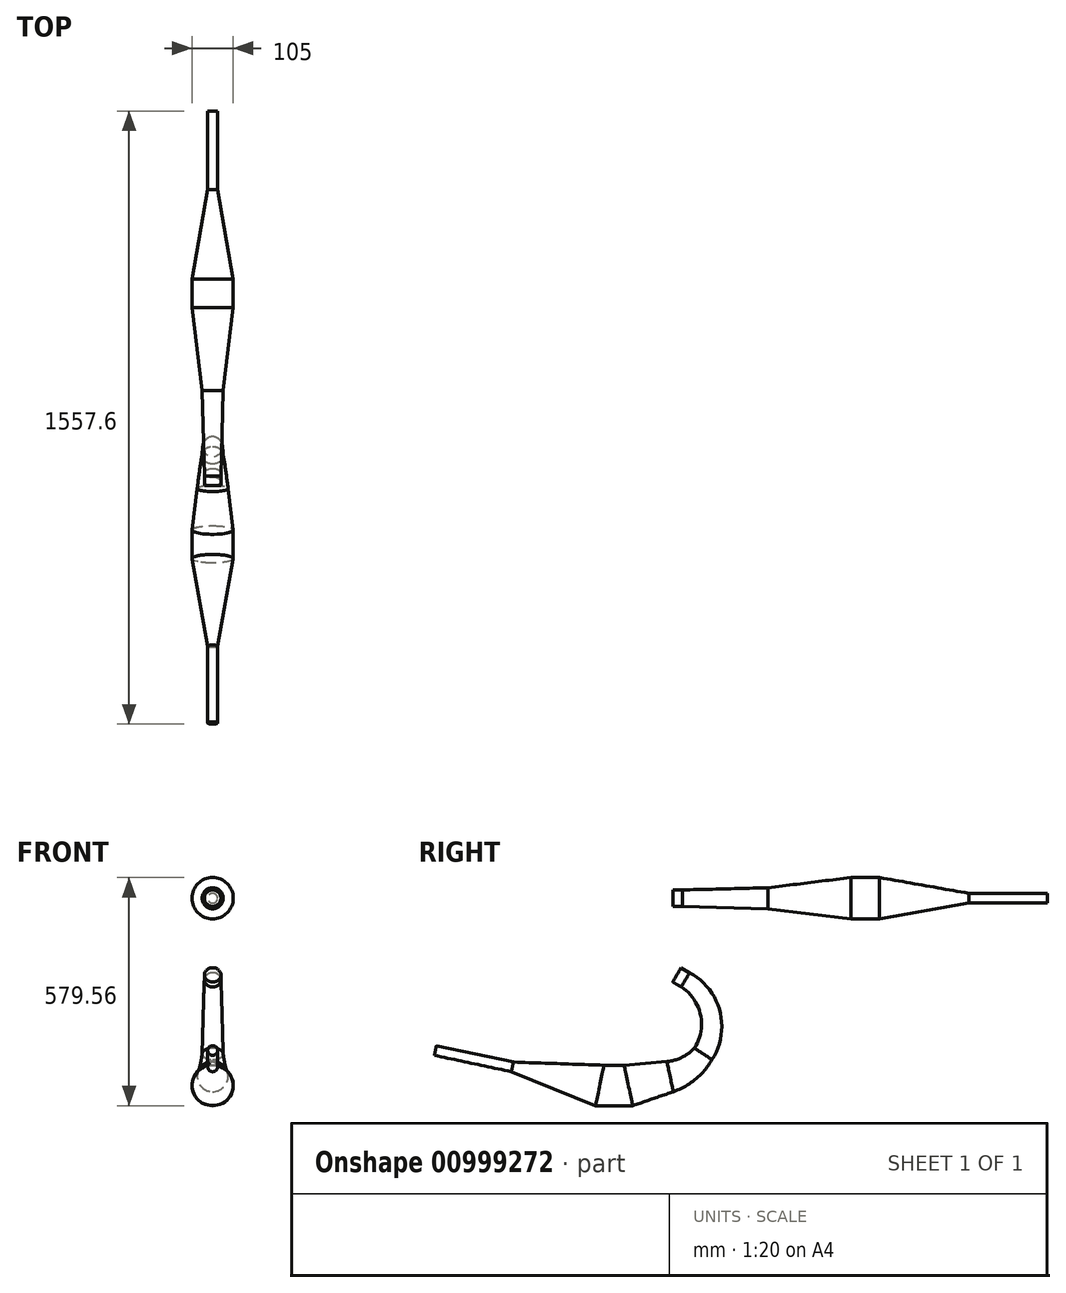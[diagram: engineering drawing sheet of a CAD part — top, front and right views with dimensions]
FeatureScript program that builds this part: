
annotation { "Feature Type Name" : "Feature", "Feature Type Description" : "" }
export const myFeature = defineFeature(function(context is Context, id is Id, definition is map)
    precondition{}
    {
        {
            var Q0;
            Q0=qCreatedBy(makeId("Right.planeOp"),FACE);
            var sketch = newSketch(context, id + "F0", { "sketchPlane" : qUnion([Q0])});
            skLineSegment(sketch, "E0", {"start": v(21.65, -12.5) * mm, "end": v(42.65, 23.87) * mm});
            skLineSegment(sketch, "E1", {"start": v(0, 191.98) * mm, "end": v(0, 233.98) * mm});
            skLineSegment(sketch, "E2", {"start": v(0, 212.98) * mm, "end": v(242, 212.98) * mm});
            skLineSegment(sketch, "E3", {"start": v(0, 212.98) * mm, "end": v(-65, 212.98) * mm});
            skLineSegment(sketch, "E4", {"start": v(242, 239.66) * mm, "end": v(242, 186.3) * mm});
            skLineSegment(sketch, "E5", {"start": v(25, 233.98) * mm, "end": v(242, 239.66) * mm});
            skLineSegment(sketch, "E6", {"start": v(25, 191.98) * mm, "end": v(242, 186.3) * mm});
            skLineSegment(sketch, "E7", {"start": v(-51.1, 50.44) * mm, "end": v(-51.1, 27.44) * mm});
            skLineSegment(sketch, "E8", {"start": v(-51.1, 38.94) * mm, "end": v(10.5, 18.19) * mm});
            skLineSegment(sketch, "E9", {"start": v(242, 212.98) * mm, "end": v(344.06, 212.98) * mm});
            skLineSegment(sketch, "E10", {"start": v(242, 239.66) * mm, "end": v(344.06, 252.2) * mm});
            skLineSegment(sketch, "E11", {"start": v(242, 186.3) * mm, "end": v(344.06, 173.76) * mm});
            skLineSegment(sketch, "E12", {"start": v(344.06, 252.2) * mm, "end": v(344.06, 173.76) * mm});
            skLineSegment(sketch, "E13", {"start": v(344.06, 212.98) * mm, "end": v(452.27, 212.98) * mm});
            skLineSegment(sketch, "E14", {"start": v(452.27, 160.48) * mm, "end": v(452.27, 265.48) * mm});
            skLineSegment(sketch, "E15", {"start": v(344.06, 252.2) * mm, "end": v(452.27, 265.48) * mm});
            skLineSegment(sketch, "E16", {"start": v(344.06, 173.76) * mm, "end": v(452.27, 160.48) * mm});
            skLineSegment(sketch, "E17", {"start": v(452.27, 212.98) * mm, "end": v(674, 212.98) * mm});
            skLineSegment(sketch, "E18", {"start": v(674, 212.98) * mm, "end": v(751.98, 212.98) * mm});
            skLineSegment(sketch, "E19", {"start": v(751.98, 200.48) * mm, "end": v(751.98, 225.48) * mm});
            skLineSegment(sketch, "E20", {"start": v(525.13, 265.48) * mm, "end": v(822.87, 212.98) * mm, "construction": true});
            skLineSegment(sketch, "E21", {"start": v(822.87, 212.98) * mm, "end": v(525.13, 160.48) * mm, "construction": true});
            skLineSegment(sketch, "E22", {"start": v(452.27, 265.48) * mm, "end": v(525.13, 265.48) * mm});
            skLineSegment(sketch, "E23", {"start": v(452.27, 160.48) * mm, "end": v(525.13, 160.48) * mm});
            skLineSegment(sketch, "E24", {"start": v(674, 186.73) * mm, "end": v(674, 239.23) * mm});
            skLineSegment(sketch, "E25", {"start": v(525.13, 265.48) * mm, "end": v(525.13, 160.48) * mm});
            skLineSegment(sketch, "E26", {"start": v(751.98, 225.48) * mm, "end": v(951.98, 225.48) * mm});
            skLineSegment(sketch, "E27", {"start": v(751.98, 200.48) * mm, "end": v(951.98, 200.48) * mm});
            skLineSegment(sketch, "E28", {"start": v(951.98, 200.48) * mm, "end": v(951.98, 225.48) * mm});
            skLineSegment(sketch, "E29", {"start": v(525.13, 265.48) * mm, "end": v(751.98, 225.48) * mm});
            skLineSegment(sketch, "E30", {"start": v(525.13, 160.48) * mm, "end": v(751.98, 200.48) * mm});
            skLineSegment(sketch, "E31", {"start": v(21.65, -12.5) * mm, "end": v(21.65, -190.3) * mm, "construction": true});
            skArc(sketch, "E32", {"start": v(32.15, 5.69) * mm, "mid": v(97.18, -130.66) * mm, "end": v(-6.8, -240.23) * mm, "construction": true});
            skLineSegment(sketch, "E33", {"start": v(-34.52, -109.8) * mm, "end": v(77.31, -182.43) * mm, "construction": true});
            skLineSegment(sketch, "E34", {"start": v(99.7, -196.96) * mm, "end": v(54.93, -167.9) * mm});
            skArc(sketch, "E35", {"start": v(99.7, -196.96) * mm, "mid": v(119.73, -74) * mm, "end": v(42.65, 23.87) * mm});
            skArc(sketch, "E36", {"start": v(54.93, -167.9) * mm, "mid": v(70.55, -83.29) * mm, "end": v(21.65, -12.5) * mm});
            skLineSegment(sketch, "E37", {"start": v(-6.8, -240.23) * mm, "end": v(-112.64, -262.73) * mm, "construction": true});
            skLineSegment(sketch, "E38", {"start": v(1.35, -278.6) * mm, "end": v(-14.95, -201.88) * mm});
            skLineSegment(sketch, "E39", {"start": v(-14.95, -201.88) * mm, "end": v(-123.56, -211.38) * mm});
            skLineSegment(sketch, "E40", {"start": v(1.35, -278.6) * mm, "end": v(-101.73, -314.08) * mm});
            skLineSegment(sketch, "E41", {"start": v(-123.56, -211.38) * mm, "end": v(-101.73, -314.08) * mm});
            skLineSegment(sketch, "E42", {"start": v(77.31, -182.43) * mm, "end": v(-6.8, -240.23) * mm, "construction": true});
            skArc(sketch, "E43", {"start": v(-14.95, -201.88) * mm, "mid": v(23.13, -191.34) * mm, "end": v(54.93, -167.9) * mm});
            skArc(sketch, "E44", {"start": v(1.35, -278.6) * mm, "mid": v(57.98, -246.75) * mm, "end": v(99.7, -196.96) * mm});
            skLineSegment(sketch, "E45", {"start": v(-112.64, -262.73) * mm, "end": v(-185.5, -262.73) * mm, "construction": true});
            skLineSegment(sketch, "E46", {"start": v(-196.42, -314.08) * mm, "end": v(-174.59, -211.38) * mm});
            skLineSegment(sketch, "E47", {"start": v(-196.42, -314.08) * mm, "end": v(-112.64, -262.73) * mm, "construction": true});
            skLineSegment(sketch, "E48", {"start": v(-185.5, -262.73) * mm, "end": v(-101.73, -314.08) * mm, "construction": true});
            skLineSegment(sketch, "E49", {"start": v(-174.59, -211.38) * mm, "end": v(-123.56, -211.38) * mm});
            skLineSegment(sketch, "E50", {"start": v(-101.73, -314.08) * mm, "end": v(-196.42, -314.08) * mm});
            skLineSegment(sketch, "E51", {"start": v(-476.74, -200.83) * mm, "end": v(-174.59, -211.38) * mm, "construction": true});
            skLineSegment(sketch, "E52", {"start": v(-476.74, -200.83) * mm, "end": v(-196.42, -314.08) * mm, "construction": true});
            skLineSegment(sketch, "E53", {"start": v(822.87, 212.98) * mm, "end": v(525.13, 212.98) * mm, "construction": true});
            skLineSegment(sketch, "E54", {"start": v(-185.5, -262.73) * mm, "end": v(-476.74, -200.83) * mm, "construction": true});
            skLineSegment(sketch, "E55", {"start": v(-410, -227.8) * mm, "end": v(-404.8, -203.34) * mm});
            skLineSegment(sketch, "E56", {"start": v(-404.8, -203.34) * mm, "end": v(-600.43, -161.76) * mm});
            skLineSegment(sketch, "E57", {"start": v(-600.43, -161.76) * mm, "end": v(-605.62, -186.21) * mm});
            skLineSegment(sketch, "E58", {"start": v(-605.62, -186.21) * mm, "end": v(-410, -227.8) * mm});
            skLineSegment(sketch, "E59", {"start": v(-404.8, -203.34) * mm, "end": v(-174.59, -211.38) * mm});
            skLineSegment(sketch, "E60", {"start": v(-410, -227.8) * mm, "end": v(-196.42, -314.08) * mm});
            skLineSegment(sketch, "E61", {"start": v(42.65, 23.87) * mm, "end": v(21, 36.37) * mm});
            skLineSegment(sketch, "E62", {"start": v(21, 36.37) * mm, "end": v(0, 0) * mm});
            skLineSegment(sketch, "E63", {"start": v(0, 0) * mm, "end": v(21.65, -12.5) * mm});
            skLineSegment(sketch, "E64", {"start": v(0, 212.98) * mm, "end": v(25, 212.98) * mm});
            skLineSegment(sketch, "E65", {"start": v(25, 233.98) * mm, "end": v(25, 191.98) * mm});
            skLineSegment(sketch, "E66", {"start": v(0, 233.98) * mm, "end": v(25, 233.98) * mm});
            skLineSegment(sketch, "E67", {"start": v(0, 191.98) * mm, "end": v(25, 191.98) * mm});
            skLineSegment(sketch, "E68", {"start": v(-51.1, 27.44) * mm, "end": v(0, 0) * mm});
            skLineSegment(sketch, "E69", {"start": v(-51.1, 50.44) * mm, "end": v(21, 36.37) * mm});
            skLineSegment(sketch, "E70", {"start": v(10.5, 18.19) * mm, "end": v(32.15, 5.69) * mm});
            skLineSegment(sketch, "E71", {"start": v(751.98, 212.98) * mm, "end": v(951.98, 212.98) * mm});
            skSolve(sketch);
        }
        {
            var Q0;
            {var subQ2=sQuery(id+"F0.wireOp",EDGE,"E64");Q0=makeQuery(id+"F0.imprint","IMPRINT",FACE,{"disambiguationData":[TD([[makeQuery(id+"F0.imprint","IMPRINT",EDGE,{"derivedFrom":subQ2}),1.0]])]});}
            var Q1;
            {var subQ0=sQuery(id+"F0.wireOp",EDGE,"E2");Q1=makeQuery(id+"F0.imprint","IMPRINT",FACE,{"disambiguationData":[TD([[makeQuery(id+"F0.imprint","IMPRINT",EDGE,{"derivedFrom":subQ0}),1.0]])]});}
            var Q2;
            {var subQ0=sQuery(id+"F0.wireOp",EDGE,"E9");Q2=makeQuery(id+"F0.imprint","IMPRINT",FACE,{"disambiguationData":[TD([[makeQuery(id+"F0.imprint","IMPRINT",EDGE,{"derivedFrom":subQ0}),1.0]])]});}
            var Q3;
            {var subQ0=sQuery(id+"F0.wireOp",EDGE,"E13");Q3=makeQuery(id+"F0.imprint","IMPRINT",FACE,{"disambiguationData":[TD([[makeQuery(id+"F0.imprint","IMPRINT",EDGE,{"derivedFrom":subQ0}),1.0]])]});}
            var Q4;
            {var subQ3=sQuery(id+"F0.wireOp",EDGE,"E22");Q4=makeQuery(id+"F0.imprint","IMPRINT",FACE,{"disambiguationData":[TD([[makeQuery(id+"F0.imprint","IMPRINT",EDGE,{"derivedFrom":subQ3}),-1.0]])]});}
            var Q5;
            {var subQ1=sQuery(id+"F0.wireOp",EDGE,"E17");var subQ3=sQuery(id+"F0.wireOp",EDGE,"E25");var subQ4=makeQuery(id+"F0.imprint","INTERSECT",VERTEX,{"derivedFrom":[subQ1,subQ3]});Q5=makeQuery(id+"F0.imprint","IMPRINT",FACE,{"disambiguationData":[TD([[makeQuery(id+"F0.imprint","IMPRINT",EDGE,{"disambiguationData":[TD([[subQ4,-1.0]])],"derivedFrom":subQ1}),1.0]])]});}
            var Q6;
            {var subQ0=sQuery(id+"F0.wireOp",EDGE,"E18");Q6=makeQuery(id+"F0.imprint","IMPRINT",FACE,{"disambiguationData":[TD([[makeQuery(id+"F0.imprint","IMPRINT",EDGE,{"derivedFrom":subQ0}),1.0]])]});}
            var Q7;
            {var subQ2=sQuery(id+"F0.wireOp",EDGE,"E26");Q7=makeQuery(id+"F0.imprint","IMPRINT",FACE,{"disambiguationData":[TD([[makeQuery(id+"F0.imprint","IMPRINT",EDGE,{"derivedFrom":subQ2}),-1.0]])]});}
            var Q8;
            Q8=sQuery(id+"F0.wireOp",EDGE,"E3");
            revolve(context, id + "F1", {"surfaceOperationType" : NewSurfaceOperationType.NEW, "entities" : qUnion([Q0, Q1, Q2, Q3, Q4, Q5, Q6, Q7]), "axis" : qUnion([Q8]), "revolveType" : RevolveType.FULL});
        }
        {
            var Q0;
            {var subQ0=sQuery(id+"F0.wireOp",EDGE,"E61");Q0=makeQuery(id+"F0.imprint","IMPRINT",FACE,{"disambiguationData":[TD([[makeQuery(id+"F0.imprint","IMPRINT",EDGE,{"derivedFrom":subQ0}),1.0]])]});}
            var Q1;
            Q1 = qSketchRegion(id + "FZ2qtyOIeemytTH_2", true);
            var Q2;
            Q2=sQuery(id+"F0.wireOp",EDGE,"E70");
            revolve(context, id + "F2", {"surfaceOperationType" : NewSurfaceOperationType.NEW, "entities" : qUnion([Q0, Q1]), "axis" : qUnion([Q2]), "revolveType" : RevolveType.FULL});
        }
        {
            var Q0;
            Q0=sQuery(id+"F0.wireOp",EDGE,"E34");
            var Q1;
            {var subQ0=sQuery(id+"F0.wireOp",EDGE,"E36");Q1=makeQuery(id+"F0.imprint","IMPRINT",FACE,{"disambiguationData":[TD([[makeQuery(id+"F0.imprint","IMPRINT",EDGE,{"derivedFrom":subQ0}),-1.0]])]});}
            cPlane(context, id + "F3", {"entities" : qUnion([Q0, Q1]), "cplaneType" : CPlaneType.LINE_ANGLE, "offset" : 0 * mm, "angle" : 90 * degree, "width" : 152.4 * mm, "height" : 152.4 * mm});
        }
        {
            var Q0;
            Q0=qCreatedBy(id+"F3.planeOp",FACE);
            var sketch = newSketch(context, id + "F4", { "sketchPlane" : qUnion([Q0])});
            skCircle(sketch, "E72", {"center": v(0, -164.2) * mm, "radius": 26.68 * mm});
            skSolve(sketch);
        }
        {
            var Q0;
            Q0=makeQuery(id+"F2.opRevolve","SWEPT_FACE",FACE,{"disambiguationData":[OSD([sQuery(id+"F0.wireOp",EDGE,"E0")])]});
            var Q1;
            Q1=makeQuery(id+"F4.imprint","IMPRINT",FACE,{"disambiguationData":[TD([[makeQuery(id+"F4.imprint","IMPRINT",EDGE,{"derivedFrom":sQuery(id+"F4.wireOp",EDGE,"E72")}),1.0]])]});
            var Q2;
            Q2=sQuery(id+"F0.wireOp",EDGE,"E35");
            var Q3;
            Q3=sQuery(id+"F0.wireOp",EDGE,"E36");
            loft(context, id + "F5", {"addGuides" : true, "sheetProfilesArray" : [{ "sheetProfileEntities" : qUnion([Q0]) }, { "sheetProfileEntities" : qUnion([Q1]) }], "guidesArray" : [{ "guideEntities" : qUnion([Q2]), "guideDerivativeType" : LoftGuideDerivativeType.DEFAULT, "guideDerivativeMagnitude" : 1 }, { "guideEntities" : qUnion([Q3]), "guideDerivativeType" : LoftGuideDerivativeType.DEFAULT, "guideDerivativeMagnitude" : 1 }]});
        }
        {
            var Q0;
            Q0=sQuery(id+"F0.wireOp",EDGE,"E38");
            var Q1;
            {var subQ5=sQuery(id+"F0.wireOp",EDGE,"E43");Q1=makeQuery(id+"F0.imprint","IMPRINT",FACE,{"disambiguationData":[TD([[makeQuery(id+"F0.imprint","IMPRINT",EDGE,{"derivedFrom":subQ5}),-1.0]])]});}
            cPlane(context, id + "F6", {"entities" : qUnion([Q0, Q1]), "cplaneType" : CPlaneType.LINE_ANGLE, "offset" : 25.4 * mm, "angle" : 90 * degree, "width" : 152.4 * mm, "height" : 152.4 * mm});
        }
        {
            var Q0;
            Q0=qCreatedBy(id+"F6.planeOp",FACE);
            var sketch = newSketch(context, id + "F7", { "sketchPlane" : qUnion([Q0])});
            skCircle(sketch, "E73", {"center": v(0, -233.57) * mm, "radius": 39.21 * mm});
            skSolve(sketch);
        }
        {
            var Q1;
            Q1=makeQuery(id+"F5.opLoft","CAP_FACE",FACE,{"disambiguationData":[OSD([makeQuery(id+"F4.imprint","IMPRINT",FACE,{"disambiguationData":[TD([[makeQuery(id+"F4.imprint","IMPRINT",EDGE,{"derivedFrom":sQuery(id+"F4.wireOp",EDGE,"E72")}),1.0]])]})])],"isStart":true});
            var Q2;
            Q2=makeQuery(id+"F7.imprint","IMPRINT",FACE,{"disambiguationData":[TD([[makeQuery(id+"F7.imprint","IMPRINT",EDGE,{"derivedFrom":sQuery(id+"F7.wireOp",EDGE,"E73")}),1.0]])]});
            var Q3;
            Q3=sQuery(id+"F0.wireOp",EDGE,"E43");
            var Q4;
            Q4=sQuery(id+"F0.wireOp",EDGE,"E44");
            loft(context, id + "F8", {"addGuides" : true, "sheetProfilesArray" : [{ "sheetProfileEntities" : qUnion([Q1]) }, { "sheetProfileEntities" : qUnion([Q2]) }], "guidesArray" : [{ "guideEntities" : qUnion([Q3]), "guideDerivativeType" : LoftGuideDerivativeType.DEFAULT, "guideDerivativeMagnitude" : 1 }, { "guideEntities" : qUnion([Q4]), "guideDerivativeType" : LoftGuideDerivativeType.DEFAULT, "guideDerivativeMagnitude" : 1 }]});
        }
        {
            var Q0;
            Q0=sQuery(id+"F0.wireOp",EDGE,"E41");
            var Q1;
            {var subQ0=sQuery(id+"F0.wireOp",EDGE,"E37");Q1=makeQuery(id+"F0.imprint","IMPRINT",FACE,{"disambiguationData":[TD([[makeQuery(id+"F0.imprint","IMPRINT",EDGE,{"derivedFrom":subQ0}),-1.0]])]});}
            cPlane(context, id + "F9", {"entities" : qUnion([Q0, Q1]), "cplaneType" : CPlaneType.LINE_ANGLE, "offset" : 25.4 * mm, "angle" : 90 * degree, "oppositeDirection" : true, "width" : 152.4 * mm, "height" : 152.4 * mm});
        }
        {
            var Q0;
            Q0=qCreatedBy(id+"F9.planeOp",FACE);
            var sketch = newSketch(context, id + "F10", { "sketchPlane" : qUnion([Q0])});
            skCircle(sketch, "E74", {"center": v(0, -233.57) * mm, "radius": 52.5 * mm});
            skSolve(sketch);
        }
        {
            var Q1;
            Q1=makeQuery(id+"F8.opLoft","CAP_FACE",FACE,{"disambiguationData":[OSD([makeQuery(id+"F7.imprint","IMPRINT",FACE,{"disambiguationData":[TD([[makeQuery(id+"F7.imprint","IMPRINT",EDGE,{"derivedFrom":sQuery(id+"F7.wireOp",EDGE,"E73")}),1.0]])]})])],"isStart":true});
            var Q2;
            Q2=makeQuery(id+"F10.imprint","IMPRINT",FACE,{"disambiguationData":[TD([[makeQuery(id+"F10.imprint","IMPRINT",EDGE,{"derivedFrom":sQuery(id+"F10.wireOp",EDGE,"E74")}),1.0]])]});
            loft(context, id + "F11", {"sheetProfilesArray" : [{ "sheetProfileEntities" : qUnion([Q1]) }, { "sheetProfileEntities" : qUnion([Q2]) }]});
        }
        {
            var Q0;
            Q0=sQuery(id+"F0.wireOp",EDGE,"E46");
            var Q1;
            {var subQ0=sQuery(id+"F0.wireOp",EDGE,"E45");Q1=makeQuery(id+"F0.imprint","IMPRINT",FACE,{"disambiguationData":[TD([[makeQuery(id+"F0.imprint","IMPRINT",EDGE,{"derivedFrom":subQ0}),-1.0]])]});}
            cPlane(context, id + "F12", {"entities" : qUnion([Q0, Q1]), "cplaneType" : CPlaneType.LINE_ANGLE, "offset" : 25.4 * mm, "angle" : 90 * degree, "width" : 152.4 * mm, "height" : 152.4 * mm});
        }
        {
            var Q0;
            Q0=qCreatedBy(id+"F12.planeOp",FACE);
            var sketch = newSketch(context, id + "F13", { "sketchPlane" : qUnion([Q0])});
            skCircle(sketch, "E75", {"center": v(0, -295.56) * mm, "radius": 52.5 * mm});
            skSolve(sketch);
        }
        {
            var Q0;
            Q0=makeQuery(id+"F11.opLoft","CAP_FACE",FACE,{"disambiguationData":[OSD([makeQuery(id+"F10.imprint","IMPRINT",FACE,{"disambiguationData":[TD([[makeQuery(id+"F10.imprint","IMPRINT",EDGE,{"derivedFrom":sQuery(id+"F10.wireOp",EDGE,"E74")}),1.0]])]})])],"isStart":true});
            var Q1;
            Q1=makeQuery(id+"F13.imprint","IMPRINT",FACE,{"disambiguationData":[TD([[makeQuery(id+"F13.imprint","IMPRINT",EDGE,{"derivedFrom":sQuery(id+"F13.wireOp",EDGE,"E75")}),1.0]])]});
            loft(context, id + "F14", {"sheetProfilesArray" : [{ "sheetProfileEntities" : qUnion([Q0]) }, { "sheetProfileEntities" : qUnion([Q1]) }]});
        }
        {
            var Q0;
            Q0=sQuery(id+"F0.wireOp",EDGE,"E55");
            cPlane(context, id + "F15", {"entities" : qUnion([Q0]), "cplaneType" : CPlaneType.LINE_ANGLE, "offset" : 25.4 * mm, "angle" : 90 * degree, "oppositeDirection" : true, "width" : 152.4 * mm, "height" : 152.4 * mm});
        }
        {
            var Q0;
            Q0=qCreatedBy(id+"F15.planeOp",FACE);
            var sketch = newSketch(context, id + "F16", { "sketchPlane" : qUnion([Q0])});
            skCircle(sketch, "E76", {"center": v(0, -295.56) * mm, "radius": 12.5 * mm});
            skSolve(sketch);
        }
        {
            var Q1;
            Q1=makeQuery(id+"F14.opLoft","CAP_FACE",FACE,{"disambiguationData":[OSD([makeQuery(id+"F13.imprint","IMPRINT",FACE,{"disambiguationData":[TD([[makeQuery(id+"F13.imprint","IMPRINT",EDGE,{"derivedFrom":sQuery(id+"F13.wireOp",EDGE,"E75")}),1.0]])]})])],"isStart":true});
            var Q2;
            Q2=makeQuery(id+"F16.imprint","IMPRINT",FACE,{"disambiguationData":[TD([[makeQuery(id+"F16.imprint","IMPRINT",EDGE,{"derivedFrom":sQuery(id+"F16.wireOp",EDGE,"E76")}),1.0]])]});
            loft(context, id + "F17", {"sheetProfilesArray" : [{ "sheetProfileEntities" : qUnion([Q1]) }, { "sheetProfileEntities" : qUnion([Q2]) }]});
        }
        {
            var Q0;
            Q0=makeQuery(id+"F17.opLoft","CAP_FACE",FACE,{"disambiguationData":[OSD([makeQuery(id+"F16.imprint","IMPRINT",FACE,{"disambiguationData":[TD([[makeQuery(id+"F16.imprint","IMPRINT",EDGE,{"derivedFrom":sQuery(id+"F16.wireOp",EDGE,"E76")}),1.0]])]})])],"isStart":true});
            extrude(context, id + "F18", {"entities" : qUnion([Q0]), "depth" : 200 * mm, "offsetDistance" : 25.4 * mm});
        }
    });
